# Revit family: IS_Nora_B9332_BIM_DE
name_source: partatom
category: Plumbing Fixtures
revit_build: Autodesk Revit MEP 2016 (Build: 20161004_0715(x64)
units: mm (PartAtom-declared; Revit-internal decimal feet)

## family parameters
Always vertical = No
Cut with Voids When Loaded = No
OmniClass Number = 23.45.55.17
OmniClass Title = Mixing Faucets
Part Type = Normal
Room Calculation Point = No
Round Connector Dimension = Use Diameter
Shared = No
Work Plane-Based = No

## types (2) — shared parameters
Accessories = www.idealstandard.de\ersatzteile
AssetType = Fixed
BIMobject category = Taps & Mixers
BOSUseNativeGeometries = 1
Brand = Ideal Standard
Brand url = http://www.idealstandard.de
CodePerformance = 0
ConnectionType = Plumbing
CurrencyUnit = €
CurrentRevision = 1
Date of publishing = 20/12/2017
DurationUnit = Year
Edition number = 1
ExpectedLife = 25
IFC Classification = Sanitary Terminal
IfcExportAs = IfcSanitaryTerminalType
Installation instructions = http://www.idealstandard.de
InstallationInstructions = www.idealstandard.de\produkte
MaintenanceInformation = www.idealstandard.de\produkte
Manufacturer name = Ideal Standard
ManufacturerURL = http://www.idealstandard.de
Material = Brass
Material main = Brass
NBS Reference Code = 35-79-79
NBS Reference Description = Sink Water Supply Fittings
NettWeight = 1.9 Kg
NominalDepth = 241 mm
NominalHeight = 297 mm
NominalLength = 241 mm
NominalWidth = 106 mm
OmniClass Code = 23-31 11 00
OmniClass Description = Faucets
Product Guid = 2b7fc539-0801-4c93-9394-17d3d2aa32ca
Product SKU = B9332
Product data url = https://bimobject.com
Product family = Sanitary
Product group = Kitchen Mixer
Product name = NORA kitchen mixer one hole single lever hand
Product url = http://www.idealstandard.de
ProductInformation = www.idealstandard.de/produkte
QR code = http://bimobject.com
Shape = Sculptured
Size = 297 x 241 x 106mm
Space = Internal
SpareParts = www.idealstandard.de/ersatzteile
Technical description = http://www.idealstandard.de
TestPressure = 10 Bar
URL = http://www.idealstandard.de
Uniclass 1.4 Code = L8212
Uniclass 1.4 Description = Fittings
Uniclass 2.0 Code = PR-35-79-79
Uniclass 2.0 Description = Sink Water Supply Fittings
Uniclass 2015 Code = Pr_40_20_87_82
Uniclass 2015 Name = Sink manual water supply sets
Uniclass2015Code = Pr_40_20_87_82
Uniclass2015Title = Sink manual water supply sets
Uniclass2015Version = Products v1.1
Version = 1
VolumeUnits = Litres
Weight Net (Kg) = 1.9
zero-valued in all types: Cost, InletConnectionSize, Nominal height, Nominal width

## per-type parameters (varying)
| type | BIMObjectName | BarCode | Color | Description | EAN code | Features | Finish | MainColor | Model | ModelNumber | ModelReference | Name |
| B9332AA - NORA kitchen mixer one hole single lever hand | ISI_IdealStandard_SinkManualWaterSupplySets_Nora_B9332AA | 3800861021773 | Chrome | IS Küchenarmatur NORA für Vorfenstermontage Chrom | https://3800861021773 | IS Küchenarmatur NORA für Vorfenstermontage Chrom | Chrome | Chrome | B9332AA | B9332AA | IS Küchenarmatur NORA für Vorfenstermontage Chrom | SinkManualWaterSupplySets_Nora_B9332AA |
| B9332GN - NORA kitchen mixer one hole single lever hand | ISI_IdealStandard_SinkManualWaterSupplySets_Nora_B9332GN | 3800861021827 | Ultra Steel | IS Küchenarmatur NORA für Vorfenstermontage Edelstahl | https://3800861021827 | IS Küchenarmatur NORA für Vorfenstermontage Edelstahl | Ultra Steel | Ultra Steel | B9332GN | B9332GN | IS Küchenarmatur NORA für Vorfenstermontage Edelstahl | SinkManualWaterSupplySets_Nora_B9332GN |

## geometry (parser evidence)
native form markers: Blend x4, Sweep x2
no freeform markers — native parametric forms only
